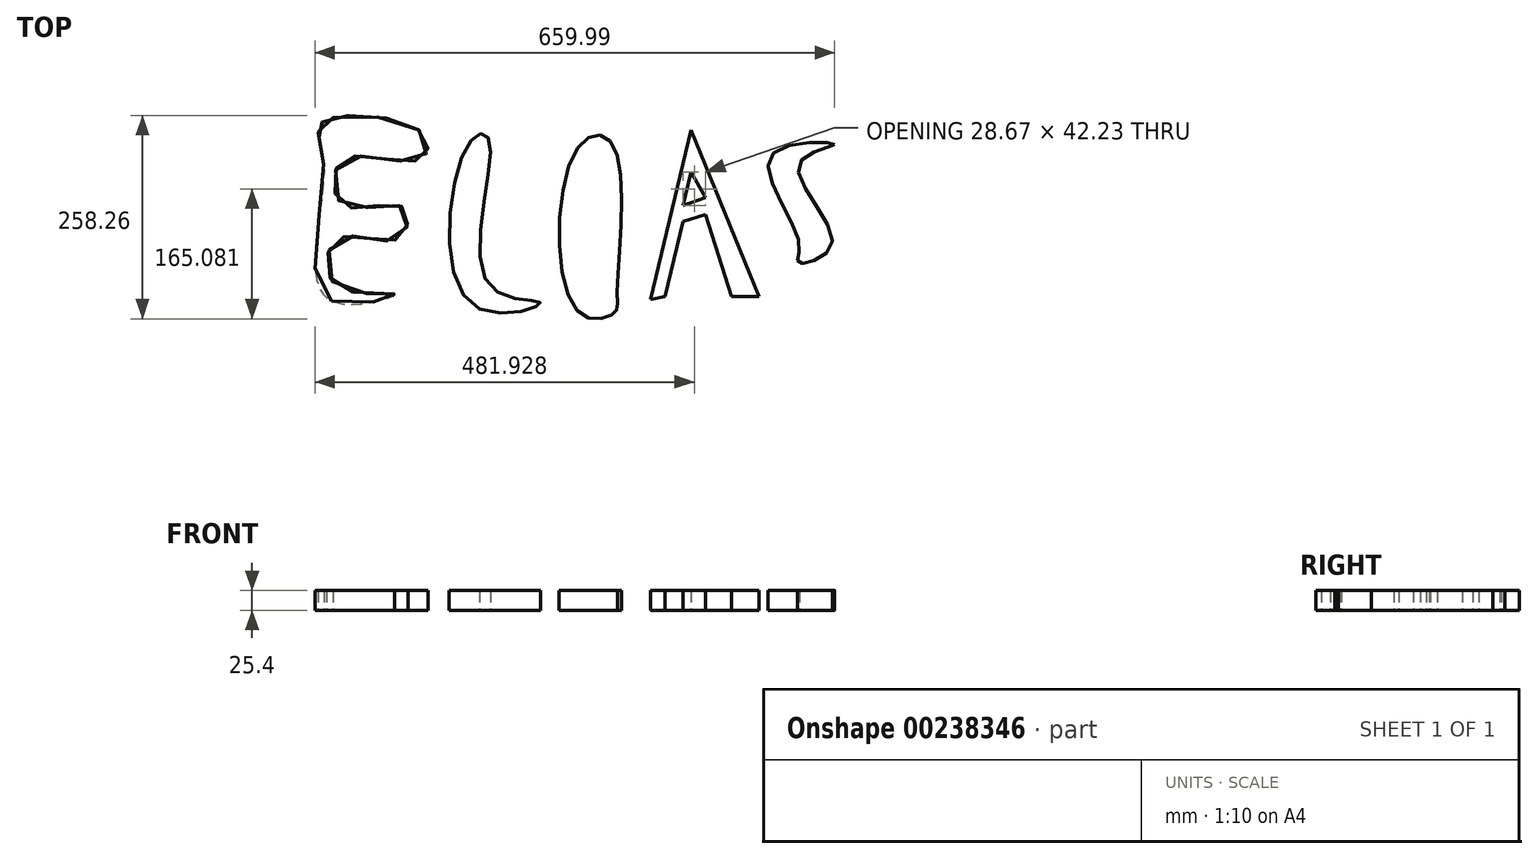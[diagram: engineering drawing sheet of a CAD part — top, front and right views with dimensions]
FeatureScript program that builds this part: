
annotation { "Feature Type Name" : "Feature", "Feature Type Description" : "" }
export const myFeature = defineFeature(function(context is Context, id is Id, definition is map)
    precondition{}
    {
        {
            var Q0;
            Q0=qCreatedBy(makeId("Top.planeOp"),FACE);
            var sketch = newSketch(context, id + "F0", { "sketchPlane" : qUnion([Q0])});
            skFitSpline(sketch, "E0", {"points": [v(-603.66, 475.87) * mm, v(-598.07, 304.56) * mm, v(-513.48, 310.18) * mm, v(-587.58, 321.34) * mm, v(-584.09, 381.48) * mm, v(-508.59, 380.8) * mm, v(-503.7, 421.36) * mm, v(-578.5, 423.43) * mm, v(-579.2, 480.77) * mm, v(-482.72, 480.8) * mm, v(-479.93, 516.46) * mm, v(-605.06, 529.7) * mm, v(-603.66, 475.87) * mm]});
            skSolve(sketch);
        }
        {
            var Q0;
            Q0=makeQuery(id+"F0.imprint","IMPRINT",FACE,{"disambiguationData":[TD([[makeQuery(id+"F0.imprint","IMPRINT",EDGE,{"derivedFrom":sQuery(id+"F0.wireOp",EDGE,"E0")}),1.0]])]});
            extrude(context, id + "F1", {"entities" : qUnion([Q0]), "depth" : 25.4 * mm});
        }
        {
            var Q0;
            Q0=qCreatedBy(makeId("Top.planeOp"),FACE);
            var sketch = newSketch(context, id + "F2", { "sketchPlane" : qUnion([Q0])});
            skFitSpline(sketch, "E1", {"points": [v(-416.76, 505.9) * mm, v(-415.36, 297.75) * mm, v(-328.45, 299.15) * mm, v(-394.33, 322.98) * mm, v(-393.63, 506.6) * mm, v(-416.76, 505.9) * mm]});
            skSolve(sketch);
        }
        {
            var Q0;
            Q0=makeQuery(id+"F2.imprint","IMPRINT",FACE,{"disambiguationData":[TD([[makeQuery(id+"F2.imprint","IMPRINT",EDGE,{"derivedFrom":sQuery(id+"F2.wireOp",EDGE,"E1")}),1.0]])]});
            extrude(context, id + "F3", {"entities" : qUnion([Q0]), "depth" : 25.4 * mm});
        }
        {
            var Q0;
            Q0=qCreatedBy(makeId("Top.planeOp"),FACE);
            var sketch = newSketch(context, id + "F4", { "sketchPlane" : qUnion([Q0])});
            skFitSpline(sketch, "E2", {"points": [v(-281.5, 496.1) * mm, v(-280.8, 288.64) * mm, v(-234.53, 286.53) * mm, v(-231.03, 311.77) * mm, v(-236.64, 501) * mm, v(-281.5, 496.1) * mm]});
            skSolve(sketch);
        }
        {
            var Q0;
            Q0=makeQuery(id+"F4.imprint","IMPRINT",FACE,{"disambiguationData":[TD([[makeQuery(id+"F4.imprint","IMPRINT",EDGE,{"derivedFrom":sQuery(id+"F4.wireOp",EDGE,"E2")}),1.0]])]});
            extrude(context, id + "F5", {"entities" : qUnion([Q0]), "depth" : 25.4 * mm});
        }
        {
            var Q0;
            Q0=qCreatedBy(makeId("Top.planeOp"),FACE);
            var sketch = newSketch(context, id + "F6", { "sketchPlane" : qUnion([Q0])});
            skLineSegment(sketch, "E3", {"start": v(-188.76, 303.47) * mm, "end": v(-137.18, 519.07) * mm});
            skLineSegment(sketch, "E4", {"start": v(-137.18, 519.07) * mm, "end": v(-50.53, 307.6) * mm});
            skLineSegment(sketch, "E5", {"start": v(-50.53, 307.6) * mm, "end": v(-85.6, 307.6) * mm});
            skLineSegment(sketch, "E6", {"start": v(-85.6, 307.6) * mm, "end": v(-118.62, 411.79) * mm});
            skLineSegment(sketch, "E7", {"start": v(-118.62, 411.79) * mm, "end": v(-147.29, 402.7) * mm});
            skLineSegment(sketch, "E8", {"start": v(-147.29, 402.7) * mm, "end": v(-170.04, 307.6) * mm});
            skLineSegment(sketch, "E9", {"start": v(-170.04, 307.6) * mm, "end": v(-188.76, 303.47) * mm});
            skLineSegment(sketch, "E10", {"start": v(-147.29, 423.14) * mm, "end": v(-137.18, 465.37) * mm});
            skLineSegment(sketch, "E11", {"start": v(-137.18, 465.37) * mm, "end": v(-118.62, 433.45) * mm});
            skLineSegment(sketch, "E12", {"start": v(-118.62, 433.45) * mm, "end": v(-147.29, 423.14) * mm});
            skSolve(sketch);
        }
        {
            var Q0;
            Q0=makeQuery(id+"F6.imprint","IMPRINT",FACE,{"disambiguationData":[TD([[makeQuery(id+"F6.imprint","IMPRINT",EDGE,{"derivedFrom":sQuery(id+"F6.wireOp",EDGE,"E3")}),-1.0]])]});
            extrude(context, id + "F7", {"entities" : qUnion([Q0]), "depth" : 25.4 * mm});
        }
        {
            var Q0;
            Q0=qCreatedBy(makeId("Top.planeOp"),FACE);
            var sketch = newSketch(context, id + "F8", { "sketchPlane" : qUnion([Q0])});
            skFitSpline(sketch, "E13", {"points": [v(45.1, 500.84) * mm, v(0, 476.25) * mm, v(42.02, 374.8) * mm, v(0, 350.2) * mm, v(0, 376.34) * mm, v(-34.83, 487) * mm, v(45.1, 500.84) * mm]});
            skSolve(sketch);
        }
        {
            var Q0;
            Q0=makeQuery(id+"F8.imprint","IMPRINT",FACE,{"disambiguationData":[TD([[makeQuery(id+"F8.imprint","IMPRINT",EDGE,{"derivedFrom":sQuery(id+"F8.wireOp",EDGE,"E13")}),-1.0]])]});
            extrude(context, id + "F9", {"entities" : qUnion([Q0]), "depth" : 25.4 * mm});
        }
    });
